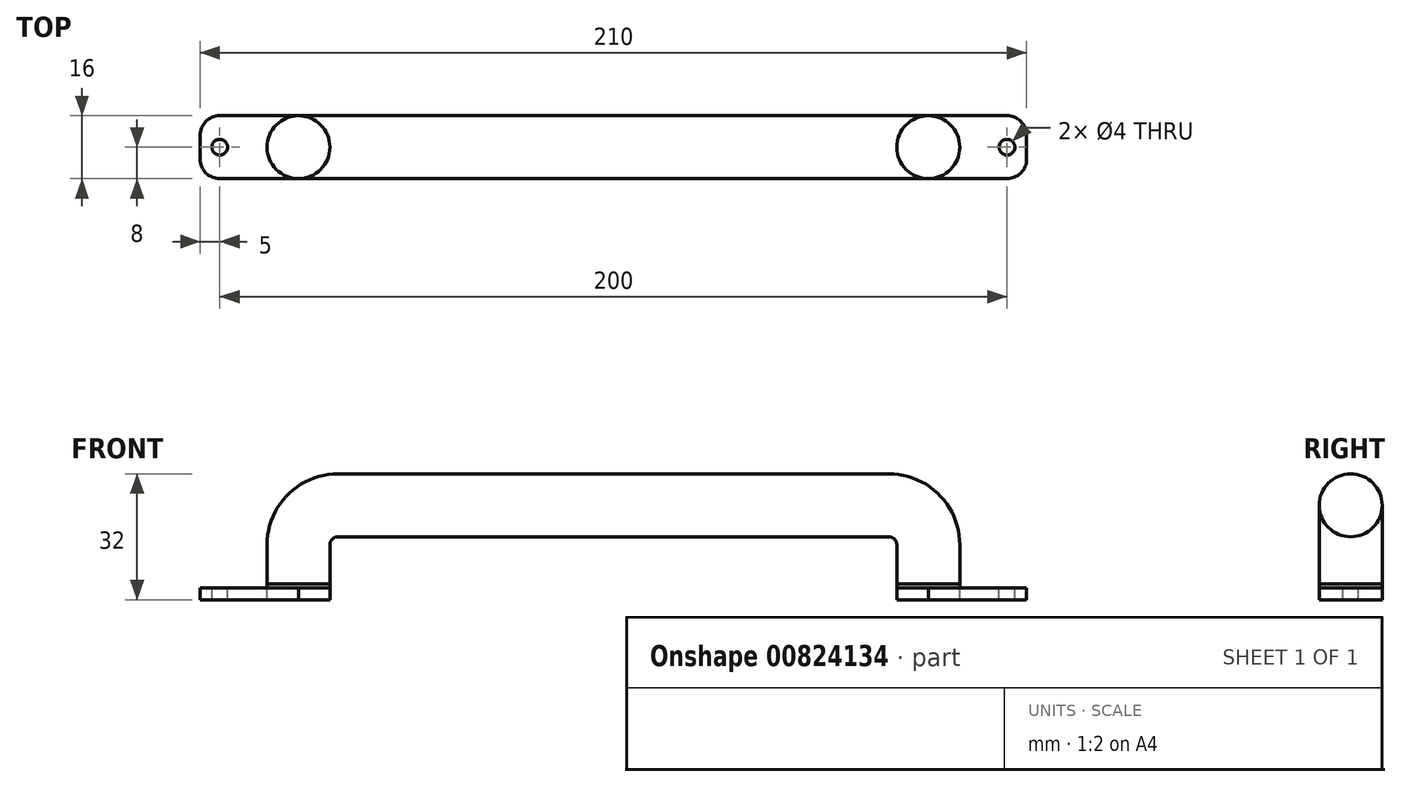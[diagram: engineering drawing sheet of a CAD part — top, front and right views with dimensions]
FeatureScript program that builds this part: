
annotation { "Feature Type Name" : "Feature", "Feature Type Description" : "" }
export const myFeature = defineFeature(function(context is Context, id is Id, definition is map)
    precondition{}
    {
        {
            var Q0;
            Q0=qCreatedBy(makeId("Top.planeOp"),FACE);
            var sketch = newSketch(context, id + "F0", { "sketchPlane" : qUnion([Q0])});
            skLineSegment(sketch, "E0.bottom", {"start": v(105, -8) * mm, "end": v(80, -8) * mm});
            skLineSegment(sketch, "E0.top", {"start": v(105, 8) * mm, "end": v(80, 8) * mm});
            skLineSegment(sketch, "E0.left", {"start": v(105, -8) * mm, "end": v(105, 8) * mm});
            skLineSegment(sketch, "E0.right", {"start": v(-105, -8) * mm, "end": v(-105, 8) * mm});
            skCircle(sketch, "E1", {"center": v(-100, 0) * mm, "radius": 2 * mm});
            skCircle(sketch, "E2", {"center": v(100, 0) * mm, "radius": 2 * mm});
            skLineSegment(sketch, "E3.trimOffspring", {"start": v(-80, 8) * mm, "end": v(-105, 8) * mm});
            skLineSegment(sketch, "E4.trimOffspring", {"start": v(-80, -8) * mm, "end": v(-105, -8) * mm});
            skCircle(sketch, "E5", {"center": v(-80, 0) * mm, "radius": 8 * mm});
            skCircle(sketch, "E6", {"center": v(80, 0) * mm, "radius": 8 * mm});
            skSolve(sketch);
        }
        {
            var Q0;
            {var subQ0=sQuery(id+"F0.wireOp",EDGE,"E5");var subQ1=makeQuery(id+"F0.imprint","INTERSECT",VERTEX,{"derivedFrom":[sQuery(id+"F0.wireOp",EDGE,"E3.trimOffspring"),subQ0]});Q0=makeQuery(id+"F0.imprint","IMPRINT",FACE,{"disambiguationData":[TD([[makeQuery(id+"F0.imprint","IMPRINT",EDGE,{"disambiguationData":[TD([[subQ1,-1.0]])],"derivedFrom":subQ0}),1.0]])]});}
            var Q1;
            {var subQ0=sQuery(id+"F0.wireOp",EDGE,"E6");var subQ1=makeQuery(id+"F0.imprint","INTERSECT",VERTEX,{"derivedFrom":[sQuery(id+"F0.wireOp",EDGE,"E0.top"),subQ0]});Q1=makeQuery(id+"F0.imprint","IMPRINT",FACE,{"disambiguationData":[TD([[makeQuery(id+"F0.imprint","IMPRINT",EDGE,{"disambiguationData":[TD([[subQ1,1.0]])],"derivedFrom":subQ0}),1.0]])]});}
            var Q2;
            Q2=sQuery(id+"F0.wireOp",EDGE,"E5");
            var Q3;
            Q3=sQuery(id+"F0.wireOp",EDGE,"E6");
            extrude(context, id + "F1", {"entities" : qUnion([Q0, Q1]), "surfaceEntities" : qUnion([Q2, Q3]), "depth" : 1 * mm, "offsetDistance" : 25 * mm});
        }
        {
            var Q0;
            Q0=makeQuery(id+"F0.imprint","IMPRINT",FACE,{"disambiguationData":[TD([[makeQuery(id+"F0.imprint","IMPRINT",EDGE,{"derivedFrom":sQuery(id+"F0.wireOp",EDGE,"E0.right")}),-1.0]])]});
            var Q1;
            {var subQ1=sQuery(id+"F0.wireOp",EDGE,"E0.bottom");Q1=makeQuery(id+"F0.imprint","IMPRINT",FACE,{"disambiguationData":[TD([[makeQuery(id+"F0.imprint","IMPRINT",EDGE,{"derivedFrom":subQ1}),-1.0]])]});}
            extrude(context, id + "F2", {"entities" : qUnion([Q0, Q1]), "oppositeDirection" : true, "depth" : 3 * mm, "offsetDistance" : 25 * mm});
        }
        {
            var Q0;
            {var subQ0=sQuery(id+"F0.wireOp",EDGE,"E5");var subQ1=makeQuery(id+"F0.imprint","INTERSECT",VERTEX,{"derivedFrom":[sQuery(id+"F0.wireOp",EDGE,"E3.trimOffspring"),subQ0]});Q0=makeQuery(id+"F0.imprint","IMPRINT",FACE,{"disambiguationData":[TD([[makeQuery(id+"F0.imprint","IMPRINT",EDGE,{"disambiguationData":[TD([[subQ1,-1.0]])],"derivedFrom":subQ0}),1.0]])]});}
            var Q1;
            {var subQ0=sQuery(id+"F0.wireOp",EDGE,"E6");var subQ1=makeQuery(id+"F0.imprint","INTERSECT",VERTEX,{"derivedFrom":[sQuery(id+"F0.wireOp",EDGE,"E0.bottom"),subQ0]});Q1=makeQuery(id+"F0.imprint","IMPRINT",FACE,{"disambiguationData":[TD([[makeQuery(id+"F0.imprint","IMPRINT",EDGE,{"disambiguationData":[TD([[subQ1,1.0]])],"derivedFrom":subQ0}),1.0]])]});}
            extrude(context, id + "F3", {"entities" : qUnion([Q0, Q1]), "oppositeDirection" : true, "depth" : 3 * mm, "offsetDistance" : 25 * mm});
        }
        {
            var Q0;
            Q0=qCreatedBy(makeId("Front.planeOp"),FACE);
            var sketch = newSketch(context, id + "F4", { "sketchPlane" : qUnion([Q0])});
            skLineSegment(sketch, "E7", {"start": v(0, 21) * mm, "end": v(70, 21) * mm});
            skLineSegment(sketch, "E8", {"start": v(0, 21) * mm, "end": v(-70, 21) * mm});
            skLineSegment(sketch, "E9", {"start": v(-80, 11) * mm, "end": v(-80, 1) * mm});
            skLineSegment(sketch, "E10", {"start": v(80, 11) * mm, "end": v(80, 1) * mm});
            skPoint(sketch, "E11.visualSharp", {"position": v(-80, 21) * mm});
            skArc(sketch, "E11.filletArc", {"start": v(-70, 21) * mm, "mid": v(-77.07, 18.07) * mm, "end": v(-80, 11) * mm});
            skPoint(sketch, "E12.visualSharp", {"position": v(80, 21) * mm});
            skArc(sketch, "E12.filletArc", {"start": v(80, 11) * mm, "mid": v(77.07, 18.07) * mm, "end": v(70, 21) * mm});
            skSolve(sketch);
        }
        {
            var Q0;
            Q0=makeQuery(id+"F1.opExtrude","CAP_FACE",FACE,{"disambiguationData":[OSD([sQuery(id+"F0.wireOp",EDGE,"E5")])],"isStart":false});
            var Q1;
            Q1=sQuery(id+"F4.wireOp",EDGE,"E9");
            var Q2;
            Q2=sQuery(id+"F4.wireOp",EDGE,"E11.filletArc");
            var Q3;
            Q3=sQuery(id+"F4.wireOp",EDGE,"E8");
            var Q4;
            Q4=sQuery(id+"F4.wireOp",EDGE,"E7");
            var Q5;
            Q5=sQuery(id+"F4.wireOp",EDGE,"E12.filletArc");
            var Q6;
            Q6=sQuery(id+"F4.wireOp",EDGE,"E10");
            sweep(context, id + "F5", {"profiles" : qUnion([Q0]), "path" : qUnion([Q1, Q2, Q3, Q4, Q5, Q6])});
        }
        {
            var Q0;
            Q0=makeQuery(id+"F2.opExtrude","SWEPT_EDGE",EDGE,{"disambiguationData":[OSD([sQuery(id+"F0.wireOp",EDGE,"E0.right"),sQuery(id+"F0.wireOp",EDGE,"E4.trimOffspring")])]});
            var Q1;
            Q1=makeQuery(id+"F2.opExtrude","SWEPT_EDGE",EDGE,{"disambiguationData":[OSD([sQuery(id+"F0.wireOp",EDGE,"E0.right"),sQuery(id+"F0.wireOp",EDGE,"E3.trimOffspring")])]});
            var Q2;
            Q2=makeQuery(id+"F2.opExtrude","SWEPT_EDGE",EDGE,{"disambiguationData":[OSD([sQuery(id+"F0.wireOp",EDGE,"E0.bottom"),sQuery(id+"F0.wireOp",EDGE,"E0.left")])]});
            var Q3;
            Q3=makeQuery(id+"F2.opExtrude","SWEPT_EDGE",EDGE,{"disambiguationData":[OSD([sQuery(id+"F0.wireOp",EDGE,"E0.top"),sQuery(id+"F0.wireOp",EDGE,"E0.left")])]});
            fillet(context, id + "F6", {"entities" : qUnion([Q0, Q1, Q2, Q3]), "radius" : 5 * mm, "tangentPropagation" : true, "allowEdgeOverflow" : false});
        }
    });
